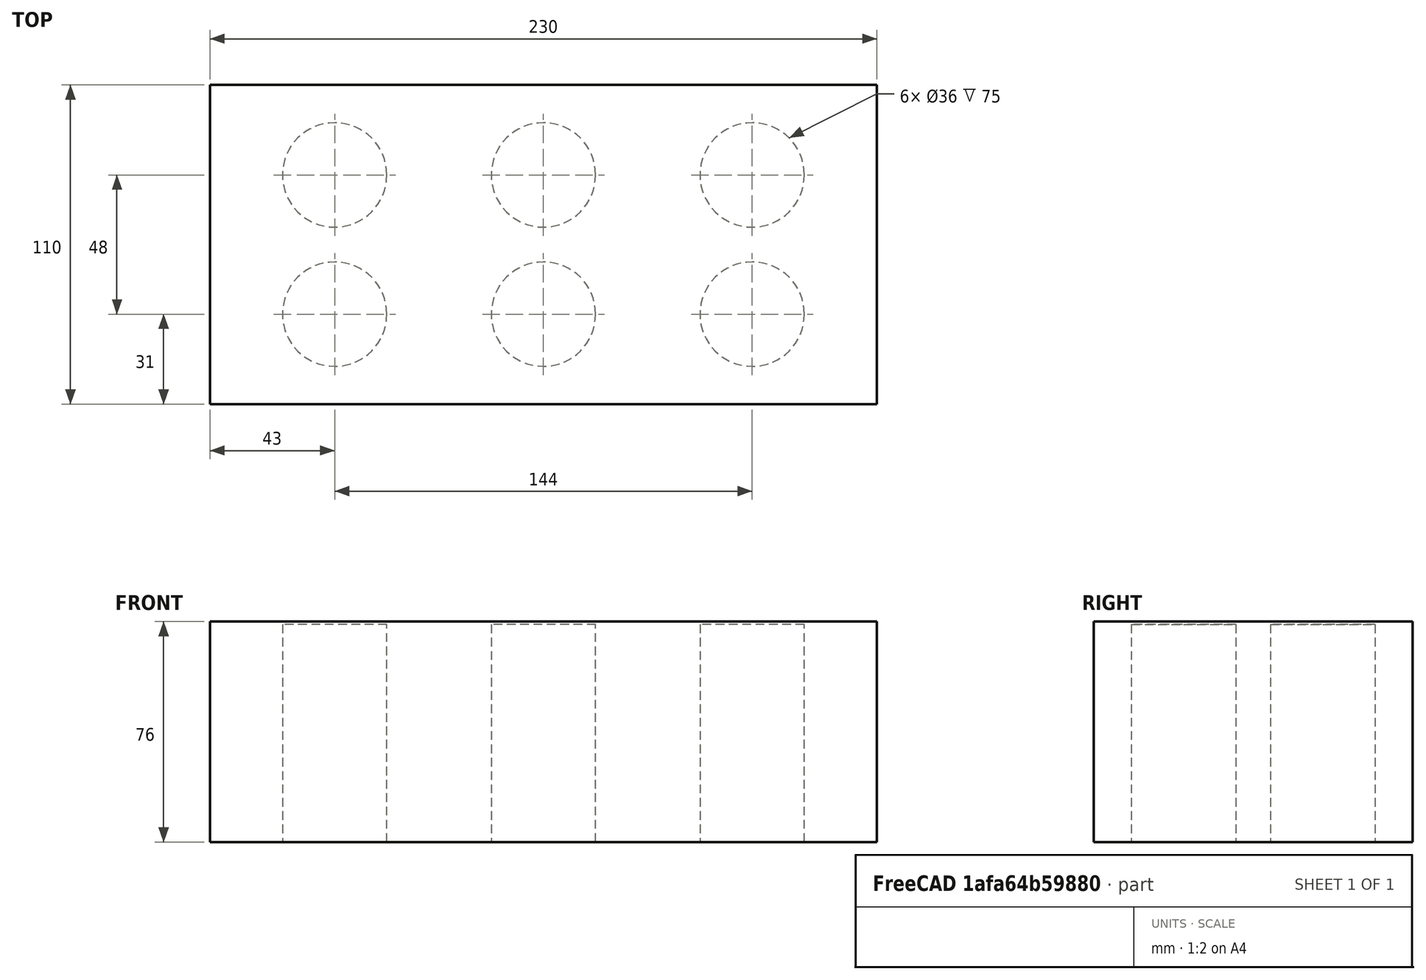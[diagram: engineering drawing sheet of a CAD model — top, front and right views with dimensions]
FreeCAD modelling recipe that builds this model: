
FCSTD DOCUMENT  (FreeCAD 0.21R33694 (Git))
Label: OJT1_T09R02_totxo
License: All rights reserved
LicenseURL: https://en.wikipedia.org/wiki/All_rights_reserved
objects: Part::Cylinder×6, Part::Box×1, Part::MultiFuse×1, Part::Cut×1
note: 9 computed .brp shape members not serialized (recipe doc carries the construction recipe); baked Part::Feature solids carry a one-line shape summary decoded from their .brp

FEATURE [Part::Box] Box  label="Base_rectangular"
  AttacherType = Attacher::AttachEngine3D
  Height = 76
  Length = 230
  Placement = pos=(0,0,1) rot=(0,0,1;0rad)
  Width = 110
FEATURE [Part::Cylinder] Cylinder  label="Forat_1"
  Angle = 360
  AttacherType = Attacher::AttachEngine3D
  FirstAngle = 0
  Height = 76
  Placement = pos=(43,31,0) rot=(0,0,1;0rad)
  Radius = 18
  SecondAngle = 0
FEATURE [Part::Cylinder] Cylinder001  label="Forat_2"
  Angle = 360
  AttacherType = Attacher::AttachEngine3D
  FirstAngle = 0
  Height = 76
  Placement = pos=(115,31,0) rot=(0,0,1;0rad)
  Radius = 18
  SecondAngle = 0
FEATURE [Part::Cylinder] Cylinder002  label="Forat_3"
  Angle = 360
  AttacherType = Attacher::AttachEngine3D
  FirstAngle = 0
  Height = 76
  Placement = pos=(187,31,0) rot=(0,0,1;0rad)
  Radius = 18
  SecondAngle = 0
FEATURE [Part::Cylinder] Cylinder003  label="Forat_4"
  Angle = 360
  AttacherType = Attacher::AttachEngine3D
  FirstAngle = 0
  Height = 76
  Placement = pos=(187,79,0) rot=(0,0,1;0rad)
  Radius = 18
  SecondAngle = 0
FEATURE [Part::Cylinder] Cylinder004  label="Forat_5"
  Angle = 360
  AttacherType = Attacher::AttachEngine3D
  FirstAngle = 0
  Height = 76
  Placement = pos=(115,79,0) rot=(0,0,1;0rad)
  Radius = 18
  SecondAngle = 0
FEATURE [Part::Cylinder] Cylinder005  label="Forat_6"
  Angle = 360
  AttacherType = Attacher::AttachEngine3D
  FirstAngle = 0
  Height = 76
  Placement = pos=(43,79,0) rot=(0,0,1;0rad)
  Radius = 18
  SecondAngle = 0
FEATURE [Part::MultiFuse] Fusion  label="Forats"
  Shapes = -> [Cylinder,Cylinder001,Cylinder002,Cylinder003,Cylinder004,Cylinder005]
FEATURE [Part::Cut] Cut  label="Totxo"
  Base = -> Box
  Tool = -> Fusion
